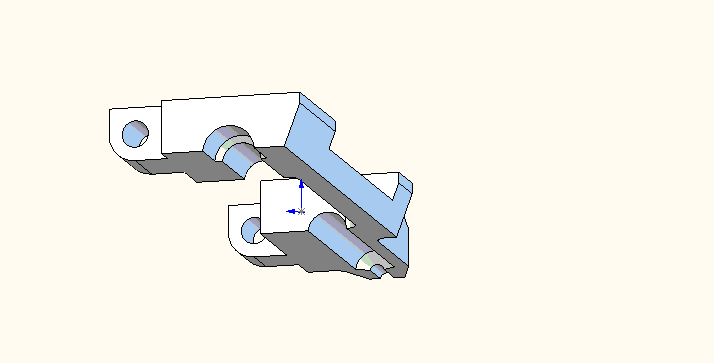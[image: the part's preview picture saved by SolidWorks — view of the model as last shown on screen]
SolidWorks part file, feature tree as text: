
SOLIDWORKS PART (.sldprt)
format: sldprt  version: not decoded by parser v0  size: 725,504 bytes
history: native  units: mm
features: sketch x15, extrude x2, cut_extrude x2, hole x2, cut_revolve x2, material x1, plane x1, fillet x1 (+11 scaffold rows collapsed)
feature tree (37):
  scaffold x11  (default folders/planes/origin — collapsed)
  material  "6061 Alloy"
  sketch  "SolidS"  dims[c1.D1=1.5875mm c1.D2=1.5875mm c1.Top_Clamp_W=~14.553214mm c1.Outer_Clamp_E=0.0mm c1.Outer_Clamp_W=0.0mm c1.Top_Clamp_H=3.556mm c1.Outer_Clamp_H=~5.111655mm c2.Outer_Clamp_H=0.0mm c2.Outer_Clamp_E=0.0mm]
  extrude  "Solid"  Depth=0mm
  sketch  "GuideClearanceS"  dims[D1=~0.79375mm D2=0.0mm D3=0.0mm]
  cut_extrude  "Guide Clearance"  [1 undecoded]
  sketch  "KevlarHoleS"  dims[D1=0.0mm]
  hole  "Kevlar Hole"  [1 undecoded]
  sketch  "HeatShrinkS"  dims[c1.D1=0.0mm c2.D1=2.54mm]
  sketch  "Sketch17"  dims[c1.D1=~6.872418mm c2.D1=59.0deg]
  cut_revolve  "Entry Chamfer"  Angle=360deg
  sketch  "Sketch5"  dims[D2=0.0mm D1=0.0mm]
  extrude  "Nose"  Depth=0mm
  sketch  "Sketch6"  dims[D1=0.0mm]
  plane  "InnerClampCenter"  Offset=0mm
  sketch  "InnerClampClearanceS"  dims[c1.D1=0.0mm c1.D2=0.0mm c2.D1=0.0mm]
  sketch  "Sketch8"  dims[D1=0.0mm]
  sketch  "Sketch9"  dims[c1.D1=~3.118356mm c2.D1=70.0deg c2.D2=3.683mm]
  sketch  "Sketch14"  dims[c1.D1=0.0508mm c1.D2=1.27mm c1.D3=3.556mm c1.D4=0.0508mm c1.D5=4.445mm c1.D6=3.8862mm c2.D4=2.921mm c2.D6=1.9558mm]
  sketch  "Sketch7"  dims[c1.D1=0.0mm c1.D2=~3.375071mm c2.D2=65.0deg c2.D1=12.7mm]
  fillet  "Fillet1"  Radius=0.79375mm
  sketch  "Sketch15"  dims[c1.D1=~1.487534mm c2.D1=45.0deg c3.D1=~1.670328mm c4.D1=59.0deg]
  cut_revolve  "Buffer Chamfer"  Angle=360deg
  sketch  "Sketch16"  dims[D1=1.016mm D2=2.286mm D3=0.762mm]
  hole  "Spring Retainer Hole"  Diameter=2.54mm
  sketch  "Sketch18"  dims[D1=0.635mm]
  cut_extrude  "Cut-Extrude1"  Depth=14.553214mm Top_Clamp_W=14.553214mm Top_Clamp_E=1.27mm Top_Clamp_H=3.556mm Outer_Clamp_W=14.553214mm
decode coverage: 22 of 24 modeling features carry decoded parameters
note: ~ marks probable driven/reference dimensions
note: 2 parameter values undecoded
summary: [note 2] (x3 features) parser:v0:name_prior (class ref resolved by constrained assignment + name prior)
note: suppression state not decoded; provenance and decode notes live in map.json
